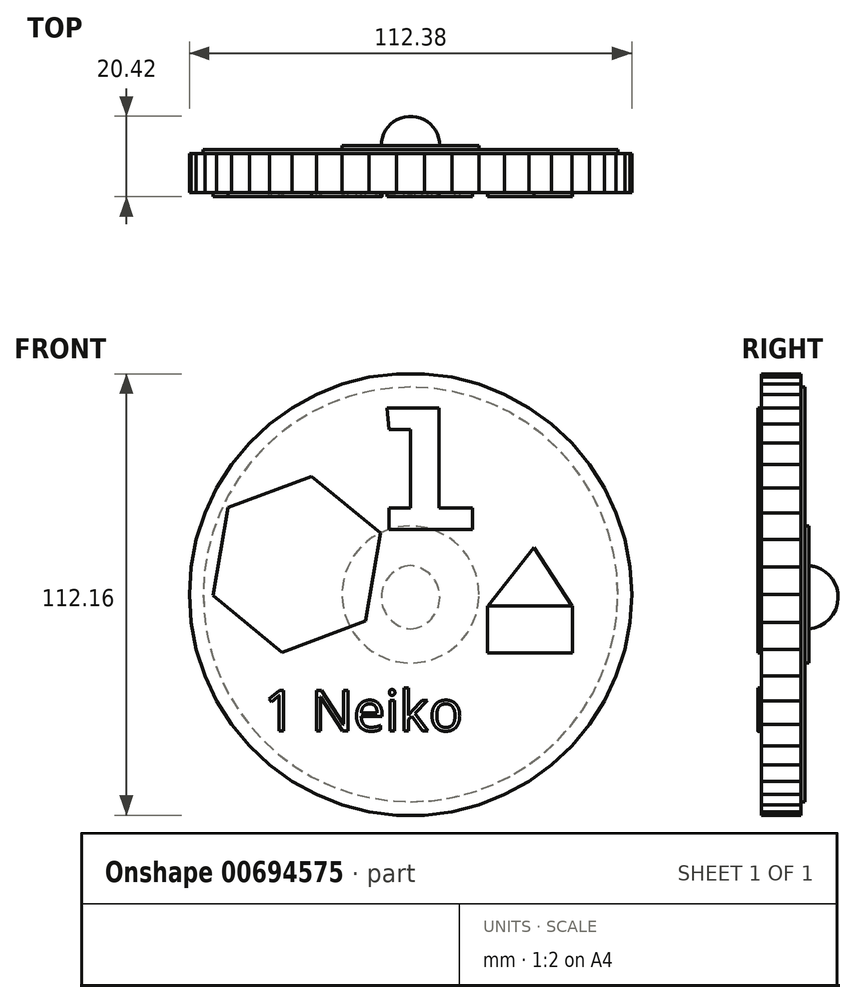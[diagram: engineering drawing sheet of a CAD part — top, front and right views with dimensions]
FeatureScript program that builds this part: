
annotation { "Feature Type Name" : "Feature", "Feature Type Description" : "" }
export const myFeature = defineFeature(function(context is Context, id is Id, definition is map)
    precondition{}
    {
        {
            var Q0;
            Q0=qCreatedBy(makeId("Front.planeOp"),FACE);
            var sketch = newSketch(context, id + "F0", { "sketchPlane" : qUnion([Q0])});
            skCircle(sketch, "E0.cCircle", {"center": v(0, 0) * mm, "radius": 56.08 * mm, "construction": true});
            skLineSegment(sketch, "E0.0", {"start": v(-3.53, 56.08) * mm, "end": v(3.53, 56.08) * mm});
            skLineSegment(sketch, "E0.1", {"start": v(3.53, 56.08) * mm, "end": v(10.53, 55.2) * mm});
            skLineSegment(sketch, "E0.2", {"start": v(10.53, 55.2) * mm, "end": v(17.36, 53.44) * mm});
            skLineSegment(sketch, "E0.3", {"start": v(17.36, 53.44) * mm, "end": v(23.93, 50.84) * mm});
            skLineSegment(sketch, "E0.4", {"start": v(23.93, 50.84) * mm, "end": v(30.1, 47.44) * mm});
            skLineSegment(sketch, "E0.5", {"start": v(30.1, 47.44) * mm, "end": v(35.82, 43.3) * mm});
            skLineSegment(sketch, "E0.6", {"start": v(35.82, 43.3) * mm, "end": v(40.96, 38.47) * mm});
            skLineSegment(sketch, "E0.7", {"start": v(40.96, 38.47) * mm, "end": v(45.46, 33.03) * mm});
            skLineSegment(sketch, "E0.8", {"start": v(45.46, 33.03) * mm, "end": v(49.24, 27.07) * mm});
            skLineSegment(sketch, "E0.9", {"start": v(49.24, 27.07) * mm, "end": v(52.25, 20.69) * mm});
            skLineSegment(sketch, "E0.10", {"start": v(52.25, 20.69) * mm, "end": v(54.43, 13.97) * mm});
            skLineSegment(sketch, "E0.11", {"start": v(54.43, 13.97) * mm, "end": v(55.75, 7.04) * mm});
            skLineSegment(sketch, "E0.12", {"start": v(55.75, 7.04) * mm, "end": v(56.2, 0) * mm});
            skLineSegment(sketch, "E0.13", {"start": v(56.2, 0) * mm, "end": v(55.75, -7.04) * mm});
            skLineSegment(sketch, "E0.14", {"start": v(55.75, -7.04) * mm, "end": v(54.43, -13.97) * mm});
            skLineSegment(sketch, "E0.15", {"start": v(54.43, -13.97) * mm, "end": v(52.25, -20.69) * mm});
            skLineSegment(sketch, "E0.16", {"start": v(52.25, -20.69) * mm, "end": v(49.24, -27.07) * mm});
            skLineSegment(sketch, "E0.17", {"start": v(49.24, -27.07) * mm, "end": v(45.46, -33.03) * mm});
            skLineSegment(sketch, "E0.18", {"start": v(45.46, -33.03) * mm, "end": v(40.96, -38.47) * mm});
            skLineSegment(sketch, "E0.19", {"start": v(40.96, -38.47) * mm, "end": v(35.82, -43.3) * mm});
            skLineSegment(sketch, "E0.20", {"start": v(35.82, -43.3) * mm, "end": v(30.1, -47.44) * mm});
            skLineSegment(sketch, "E0.21", {"start": v(30.1, -47.44) * mm, "end": v(23.93, -50.84) * mm});
            skLineSegment(sketch, "E0.22", {"start": v(23.93, -50.84) * mm, "end": v(17.36, -53.44) * mm});
            skLineSegment(sketch, "E0.23", {"start": v(17.36, -53.44) * mm, "end": v(10.53, -55.2) * mm});
            skLineSegment(sketch, "E0.24", {"start": v(10.53, -55.2) * mm, "end": v(3.53, -56.08) * mm});
            skLineSegment(sketch, "E0.25", {"start": v(3.53, -56.08) * mm, "end": v(-3.53, -56.08) * mm});
            skLineSegment(sketch, "E0.26", {"start": v(-3.53, -56.08) * mm, "end": v(-10.53, -55.2) * mm});
            skLineSegment(sketch, "E0.27", {"start": v(-10.53, -55.2) * mm, "end": v(-17.36, -53.44) * mm});
            skLineSegment(sketch, "E0.28", {"start": v(-17.36, -53.44) * mm, "end": v(-23.93, -50.84) * mm});
            skLineSegment(sketch, "E0.29", {"start": v(-23.93, -50.84) * mm, "end": v(-30.1, -47.44) * mm});
            skLineSegment(sketch, "E0.30", {"start": v(-30.1, -47.44) * mm, "end": v(-35.82, -43.3) * mm});
            skLineSegment(sketch, "E0.31", {"start": v(-35.82, -43.3) * mm, "end": v(-40.96, -38.47) * mm});
            skLineSegment(sketch, "E0.32", {"start": v(-40.96, -38.47) * mm, "end": v(-45.46, -33.03) * mm});
            skLineSegment(sketch, "E0.33", {"start": v(-45.46, -33.03) * mm, "end": v(-49.24, -27.07) * mm});
            skLineSegment(sketch, "E0.34", {"start": v(-49.24, -27.07) * mm, "end": v(-52.25, -20.69) * mm});
            skLineSegment(sketch, "E0.35", {"start": v(-52.25, -20.69) * mm, "end": v(-54.43, -13.97) * mm});
            skLineSegment(sketch, "E0.36", {"start": v(-54.43, -13.97) * mm, "end": v(-55.75, -7.04) * mm});
            skLineSegment(sketch, "E0.37", {"start": v(-55.75, -7.04) * mm, "end": v(-56.2, 0) * mm});
            skLineSegment(sketch, "E0.38", {"start": v(-56.2, 0) * mm, "end": v(-55.75, 7.04) * mm});
            skLineSegment(sketch, "E0.39", {"start": v(-55.75, 7.04) * mm, "end": v(-54.43, 13.97) * mm});
            skLineSegment(sketch, "E0.40", {"start": v(-54.43, 13.97) * mm, "end": v(-52.25, 20.69) * mm});
            skLineSegment(sketch, "E0.41", {"start": v(-52.25, 20.69) * mm, "end": v(-49.24, 27.07) * mm});
            skLineSegment(sketch, "E0.42", {"start": v(-49.24, 27.07) * mm, "end": v(-45.46, 33.03) * mm});
            skLineSegment(sketch, "E0.43", {"start": v(-45.46, 33.03) * mm, "end": v(-40.96, 38.47) * mm});
            skLineSegment(sketch, "E0.44", {"start": v(-40.96, 38.47) * mm, "end": v(-35.82, 43.3) * mm});
            skLineSegment(sketch, "E0.45", {"start": v(-35.82, 43.3) * mm, "end": v(-30.1, 47.44) * mm});
            skLineSegment(sketch, "E0.46", {"start": v(-30.1, 47.44) * mm, "end": v(-23.93, 50.84) * mm});
            skLineSegment(sketch, "E0.47", {"start": v(-23.93, 50.84) * mm, "end": v(-17.36, 53.44) * mm});
            skLineSegment(sketch, "E0.48", {"start": v(-17.36, 53.44) * mm, "end": v(-10.53, 55.2) * mm});
            skLineSegment(sketch, "E0.49", {"start": v(-10.53, 55.2) * mm, "end": v(-3.53, 56.08) * mm});
            skPoint(sketch, "E0.0.midPoint", {"position": v(0, 56.08) * mm});
            skSolve(sketch);
        }
        {
            var Q0;
            Q0 = qSketchRegion(id + "F0", true);
            extrude(context, id + "F1", {"entities" : qUnion([Q0]), "depth" : 10 * mm, "offsetDistance" : 25.4 * mm});
        }
        {
            var Q0;
            Q0=makeQuery(id+"F1.opExtrude","CAP_FACE",FACE,{"disambiguationData":[OSD([sQuery(id+"F0.wireOp",EDGE,"E0.0"),sQuery(id+"F0.wireOp",EDGE,"E0.1"),sQuery(id+"F0.wireOp",EDGE,"E0.2"),sQuery(id+"F0.wireOp",EDGE,"E0.3"),sQuery(id+"F0.wireOp",EDGE,"E0.4"),sQuery(id+"F0.wireOp",EDGE,"E0.5"),sQuery(id+"F0.wireOp",EDGE,"E0.6"),sQuery(id+"F0.wireOp",EDGE,"E0.7"),sQuery(id+"F0.wireOp",EDGE,"E0.8"),sQuery(id+"F0.wireOp",EDGE,"E0.9"),sQuery(id+"F0.wireOp",EDGE,"E0.10"),sQuery(id+"F0.wireOp",EDGE,"E0.11"),sQuery(id+"F0.wireOp",EDGE,"E0.12"),sQuery(id+"F0.wireOp",EDGE,"E0.13"),sQuery(id+"F0.wireOp",EDGE,"E0.14"),sQuery(id+"F0.wireOp",EDGE,"E0.15"),sQuery(id+"F0.wireOp",EDGE,"E0.16"),sQuery(id+"F0.wireOp",EDGE,"E0.17"),sQuery(id+"F0.wireOp",EDGE,"E0.18"),sQuery(id+"F0.wireOp",EDGE,"E0.19"),sQuery(id+"F0.wireOp",EDGE,"E0.20"),sQuery(id+"F0.wireOp",EDGE,"E0.21"),sQuery(id+"F0.wireOp",EDGE,"E0.22"),sQuery(id+"F0.wireOp",EDGE,"E0.23"),sQuery(id+"F0.wireOp",EDGE,"E0.24"),sQuery(id+"F0.wireOp",EDGE,"E0.25"),sQuery(id+"F0.wireOp",EDGE,"E0.26"),sQuery(id+"F0.wireOp",EDGE,"E0.27"),sQuery(id+"F0.wireOp",EDGE,"E0.28"),sQuery(id+"F0.wireOp",EDGE,"E0.29"),sQuery(id+"F0.wireOp",EDGE,"E0.30"),sQuery(id+"F0.wireOp",EDGE,"E0.31"),sQuery(id+"F0.wireOp",EDGE,"E0.32"),sQuery(id+"F0.wireOp",EDGE,"E0.33"),sQuery(id+"F0.wireOp",EDGE,"E0.34"),sQuery(id+"F0.wireOp",EDGE,"E0.35"),sQuery(id+"F0.wireOp",EDGE,"E0.36"),sQuery(id+"F0.wireOp",EDGE,"E0.37"),sQuery(id+"F0.wireOp",EDGE,"E0.38"),sQuery(id+"F0.wireOp",EDGE,"E0.39"),sQuery(id+"F0.wireOp",EDGE,"E0.40"),sQuery(id+"F0.wireOp",EDGE,"E0.41"),sQuery(id+"F0.wireOp",EDGE,"E0.42"),sQuery(id+"F0.wireOp",EDGE,"E0.43"),sQuery(id+"F0.wireOp",EDGE,"E0.44"),sQuery(id+"F0.wireOp",EDGE,"E0.45"),sQuery(id+"F0.wireOp",EDGE,"E0.46"),sQuery(id+"F0.wireOp",EDGE,"E0.47"),sQuery(id+"F0.wireOp",EDGE,"E0.48"),sQuery(id+"F0.wireOp",EDGE,"E0.49")])],"isStart":false});
            var sketch = newSketch(context, id + "F2", { "sketchPlane" : qUnion([Q0])});
            skLineSegment(sketch, "E1", {"start": v(-5.92, 47.44) * mm, "end": v(7.29, 47.44) * mm});
            skLineSegment(sketch, "E2", {"start": v(7.29, 47.44) * mm, "end": v(7.29, 21.93) * mm});
            skLineSegment(sketch, "E3", {"start": v(7.29, 21.93) * mm, "end": v(15.75, 21.93) * mm});
            skLineSegment(sketch, "E4", {"start": v(15.75, 21.93) * mm, "end": v(15.75, 16.57) * mm});
            skLineSegment(sketch, "E5", {"start": v(15.75, 16.57) * mm, "end": v(-5.5, 16.57) * mm});
            skLineSegment(sketch, "E6", {"start": v(-5.5, 16.57) * mm, "end": v(-5.5, 21.93) * mm});
            skLineSegment(sketch, "E7", {"start": v(-5.5, 21.93) * mm, "end": v(0, 21.93) * mm});
            skLineSegment(sketch, "E8", {"start": v(0, 21.93) * mm, "end": v(0, 41.95) * mm});
            skLineSegment(sketch, "E9", {"start": v(0, 41.95) * mm, "end": v(-5.5, 41.95) * mm});
            skLineSegment(sketch, "E10", {"start": v(-5.5, 41.95) * mm, "end": v(-5.92, 47.44) * mm});
            skSolve(sketch);
        }
        {
            var Q0;
            Q0=makeQuery(id+"F2.imprint","IMPRINT",FACE,{"disambiguationData":[TD([[makeQuery(id+"F2.imprint","IMPRINT",EDGE,{"derivedFrom":sQuery(id+"F2.wireOp",EDGE,"E1")}),1.0]])]});
            var sketch = newSketch(context, id + "F3", { "sketchPlane" : qUnion([Q0])});
            skText(sketch, "E11", { "text": "1 Neiko", "fontName": "OpenSans-Regular.ttf"});
            const initialGuessF3  = {"E11": [-0.03727, -0.03463, 1, 0, 0.01032]};
            skSetInitialGuess(sketch, initialGuessF3);
            skSolve(sketch);
        }
        {
            var Q0;
            Q0=makeQuery(id+"F2.imprint","IMPRINT",FACE,{"disambiguationData":[TD([[makeQuery(id+"F2.imprint","IMPRINT",EDGE,{"derivedFrom":sQuery(id+"F2.wireOp",EDGE,"E1")}),1.0]])]});
            var sketch = newSketch(context, id + "F4", { "sketchPlane" : qUnion([Q0])});
            skCircle(sketch, "E12.cCircle", {"center": v(-28.89, 7.66) * mm, "radius": 19.65 * mm, "construction": true});
            skLineSegment(sketch, "E12.0", {"start": v(-46.39, 22.1) * mm, "end": v(-25.13, 30.04) * mm});
            skLineSegment(sketch, "E12.1", {"start": v(-25.13, 30.04) * mm, "end": v(-7.63, 15.6) * mm});
            skLineSegment(sketch, "E12.2", {"start": v(-7.63, 15.6) * mm, "end": v(-11.39, -6.77) * mm});
            skLineSegment(sketch, "E12.3", {"start": v(-11.39, -6.77) * mm, "end": v(-32.64, -14.7) * mm});
            skLineSegment(sketch, "E12.4", {"start": v(-32.64, -14.7) * mm, "end": v(-50.14, -0.27) * mm});
            skLineSegment(sketch, "E12.5", {"start": v(-50.14, -0.27) * mm, "end": v(-46.39, 22.1) * mm});
            skPoint(sketch, "E12.0.midPoint", {"position": v(-35.76, 26.07) * mm});
            skSolve(sketch);
        }
        {
            var Q0;
            Q0=makeQuery(id+"F3.imprint","IMPRINT",FACE,{"disambiguationData":[TD([[makeQuery(id+"F3.imprint","IMPRINT",EDGE,{"derivedFrom":sQuery(id+"F3.wireOp",EDGE,"E11.sketch_text.stroke-0")}),1.0]])]});
            var sketch = newSketch(context, id + "F5", { "sketchPlane" : qUnion([Q0])});
            skLineSegment(sketch, "E13.bottom", {"start": v(19.57, -14.82) * mm, "end": v(41.14, -14.82) * mm});
            skLineSegment(sketch, "E13.top", {"start": v(19.57, -2.93) * mm, "end": v(41.14, -2.93) * mm});
            skLineSegment(sketch, "E13.left", {"start": v(19.57, -14.82) * mm, "end": v(19.57, -2.93) * mm});
            skLineSegment(sketch, "E13.right", {"start": v(41.14, -14.82) * mm, "end": v(41.14, -2.93) * mm});
            skSolve(sketch);
        }
        {
            var Q0;
            Q0=makeQuery(id+"F2.imprint","IMPRINT",FACE,{"disambiguationData":[TD([[makeQuery(id+"F2.imprint","IMPRINT",EDGE,{"derivedFrom":sQuery(id+"F2.wireOp",EDGE,"E1")}),1.0]])]});
            var sketch = newSketch(context, id + "F6", { "sketchPlane" : qUnion([Q0])});
            skLineSegment(sketch, "E14", {"start": v(19.63, -2.85) * mm, "end": v(41.06, -2.85) * mm});
            skLineSegment(sketch, "E15", {"start": v(41.06, -2.85) * mm, "end": v(31.41, 11.96) * mm});
            skLineSegment(sketch, "E16", {"start": v(31.41, 11.96) * mm, "end": v(19.63, -2.85) * mm});
            skSolve(sketch);
        }
        {
            var Q0;
            Q0=makeQuery(id+"F1.opExtrude","CAP_FACE",FACE,{"disambiguationData":[OSD([sQuery(id+"F0.wireOp",EDGE,"E0.0"),sQuery(id+"F0.wireOp",EDGE,"E0.1"),sQuery(id+"F0.wireOp",EDGE,"E0.2"),sQuery(id+"F0.wireOp",EDGE,"E0.3"),sQuery(id+"F0.wireOp",EDGE,"E0.4"),sQuery(id+"F0.wireOp",EDGE,"E0.5"),sQuery(id+"F0.wireOp",EDGE,"E0.6"),sQuery(id+"F0.wireOp",EDGE,"E0.7"),sQuery(id+"F0.wireOp",EDGE,"E0.8"),sQuery(id+"F0.wireOp",EDGE,"E0.9"),sQuery(id+"F0.wireOp",EDGE,"E0.10"),sQuery(id+"F0.wireOp",EDGE,"E0.11"),sQuery(id+"F0.wireOp",EDGE,"E0.12"),sQuery(id+"F0.wireOp",EDGE,"E0.13"),sQuery(id+"F0.wireOp",EDGE,"E0.14"),sQuery(id+"F0.wireOp",EDGE,"E0.15"),sQuery(id+"F0.wireOp",EDGE,"E0.16"),sQuery(id+"F0.wireOp",EDGE,"E0.17"),sQuery(id+"F0.wireOp",EDGE,"E0.18"),sQuery(id+"F0.wireOp",EDGE,"E0.19"),sQuery(id+"F0.wireOp",EDGE,"E0.20"),sQuery(id+"F0.wireOp",EDGE,"E0.21"),sQuery(id+"F0.wireOp",EDGE,"E0.22"),sQuery(id+"F0.wireOp",EDGE,"E0.23"),sQuery(id+"F0.wireOp",EDGE,"E0.24"),sQuery(id+"F0.wireOp",EDGE,"E0.25"),sQuery(id+"F0.wireOp",EDGE,"E0.26"),sQuery(id+"F0.wireOp",EDGE,"E0.27"),sQuery(id+"F0.wireOp",EDGE,"E0.28"),sQuery(id+"F0.wireOp",EDGE,"E0.29"),sQuery(id+"F0.wireOp",EDGE,"E0.30"),sQuery(id+"F0.wireOp",EDGE,"E0.31"),sQuery(id+"F0.wireOp",EDGE,"E0.32"),sQuery(id+"F0.wireOp",EDGE,"E0.33"),sQuery(id+"F0.wireOp",EDGE,"E0.34"),sQuery(id+"F0.wireOp",EDGE,"E0.35"),sQuery(id+"F0.wireOp",EDGE,"E0.36"),sQuery(id+"F0.wireOp",EDGE,"E0.37"),sQuery(id+"F0.wireOp",EDGE,"E0.38"),sQuery(id+"F0.wireOp",EDGE,"E0.39"),sQuery(id+"F0.wireOp",EDGE,"E0.40"),sQuery(id+"F0.wireOp",EDGE,"E0.41"),sQuery(id+"F0.wireOp",EDGE,"E0.42"),sQuery(id+"F0.wireOp",EDGE,"E0.43"),sQuery(id+"F0.wireOp",EDGE,"E0.44"),sQuery(id+"F0.wireOp",EDGE,"E0.45"),sQuery(id+"F0.wireOp",EDGE,"E0.46"),sQuery(id+"F0.wireOp",EDGE,"E0.47"),sQuery(id+"F0.wireOp",EDGE,"E0.48"),sQuery(id+"F0.wireOp",EDGE,"E0.49")])],"isStart":true});
            var sketch = newSketch(context, id + "F7", { "sketchPlane" : qUnion([Q0])});
            skCircle(sketch, "E17", {"center": v(0, 0) * mm, "radius": 52.66 * mm});
            skSolve(sketch);
        }
        {
            var Q0;
            Q0 = qSketchRegion(id + "F7", true);
            extrude(context, id + "F8", {"entities" : qUnion([Q0]), "operationType" : NewBodyOperationType.ADD, "depth" : 1 * mm, "offsetDistance" : 25.4 * mm});
        }
        {
            var Q0;
            Q0=makeQuery(id+"F8.opExtrude","CAP_FACE",FACE,{"disambiguationData":[OSD([sQuery(id+"F7.wireOp",EDGE,"E17")])],"isStart":false});
            var sketch = newSketch(context, id + "F9", { "sketchPlane" : qUnion([Q0])});
            skCircle(sketch, "E18", {"center": v(0, 0) * mm, "radius": 17.4 * mm});
            skSolve(sketch);
        }
        {
            var Q0;
            Q0 = qSketchRegion(id + "F9", true);
            extrude(context, id + "F10", {"entities" : qUnion([Q0]), "operationType" : NewBodyOperationType.ADD, "depth" : 1 * mm, "offsetDistance" : 25.4 * mm});
        }
        {
            var Q0;
            Q0=makeQuery(id+"F2.imprint","IMPRINT",FACE,{"disambiguationData":[TD([[makeQuery(id+"F2.imprint","IMPRINT",EDGE,{"derivedFrom":sQuery(id+"F2.wireOp",EDGE,"E1")}),-1.0]])]});
            var Q1;
            Q1=makeQuery(id+"F6.imprint","IMPRINT",FACE,{"disambiguationData":[TD([[makeQuery(id+"F6.imprint","IMPRINT",EDGE,{"derivedFrom":sQuery(id+"F6.wireOp",EDGE,"E14")}),1.0]])]});
            var Q2;
            Q2=makeQuery(id+"F4.imprint","IMPRINT",FACE,{"disambiguationData":[TD([[makeQuery(id+"F4.imprint","IMPRINT",EDGE,{"derivedFrom":sQuery(id+"F4.wireOp",EDGE,"E12.0")}),-1.0]])]});
            var Q3;
            Q3 = qSketchRegion(id + "F3", true);
            extrude(context, id + "F11", {"entities" : qUnion([Q0, Q1, Q2, Q3]), "operationType" : NewBodyOperationType.ADD, "depth" : 1 * mm, "offsetDistance" : 25.4 * mm});
        }
        {
            var Q0;
            Q0=makeQuery(id+"F5.imprint","IMPRINT",FACE,{"disambiguationData":[TD([[makeQuery(id+"F5.imprint","IMPRINT",EDGE,{"derivedFrom":sQuery(id+"F5.wireOp",EDGE,"E13.bottom")}),1.0]])]});
            extrude(context, id + "F12", {"entities" : qUnion([Q0]), "operationType" : NewBodyOperationType.ADD, "depth" : 1 * mm, "offsetDistance" : 25.4 * mm});
        }
        {
            var Q0;
            Q0=makeQuery(id+"F10.opExtrude","CAP_FACE",FACE,{"disambiguationData":[OSD([sQuery(id+"F9.wireOp",EDGE,"E18")])],"isStart":false});
            var sketch = newSketch(context, id + "F13", { "sketchPlane" : qUnion([Q0])});
            skArc(sketch, "E19", {"start": v(0, -8.74) * mm, "mid": v(7.42, -0.7) * mm, "end": v(0, 7.33) * mm});
            skLineSegment(sketch, "E20", {"start": v(0, 7.33) * mm, "end": v(0, -8.74) * mm});
            skSolve(sketch);
        }
        {
            var Q0;
            Q0 = qSketchRegion(id + "F13", true);
            var Q1;
            Q1=sQuery(id+"F13.wireOp",EDGE,"E20");
            revolve(context, id + "F14", {"operationType" : NewBodyOperationType.ADD, "entities" : qUnion([Q0]), "axis" : qUnion([Q1]), "revolveType" : RevolveType.FULL});
        }
    });
